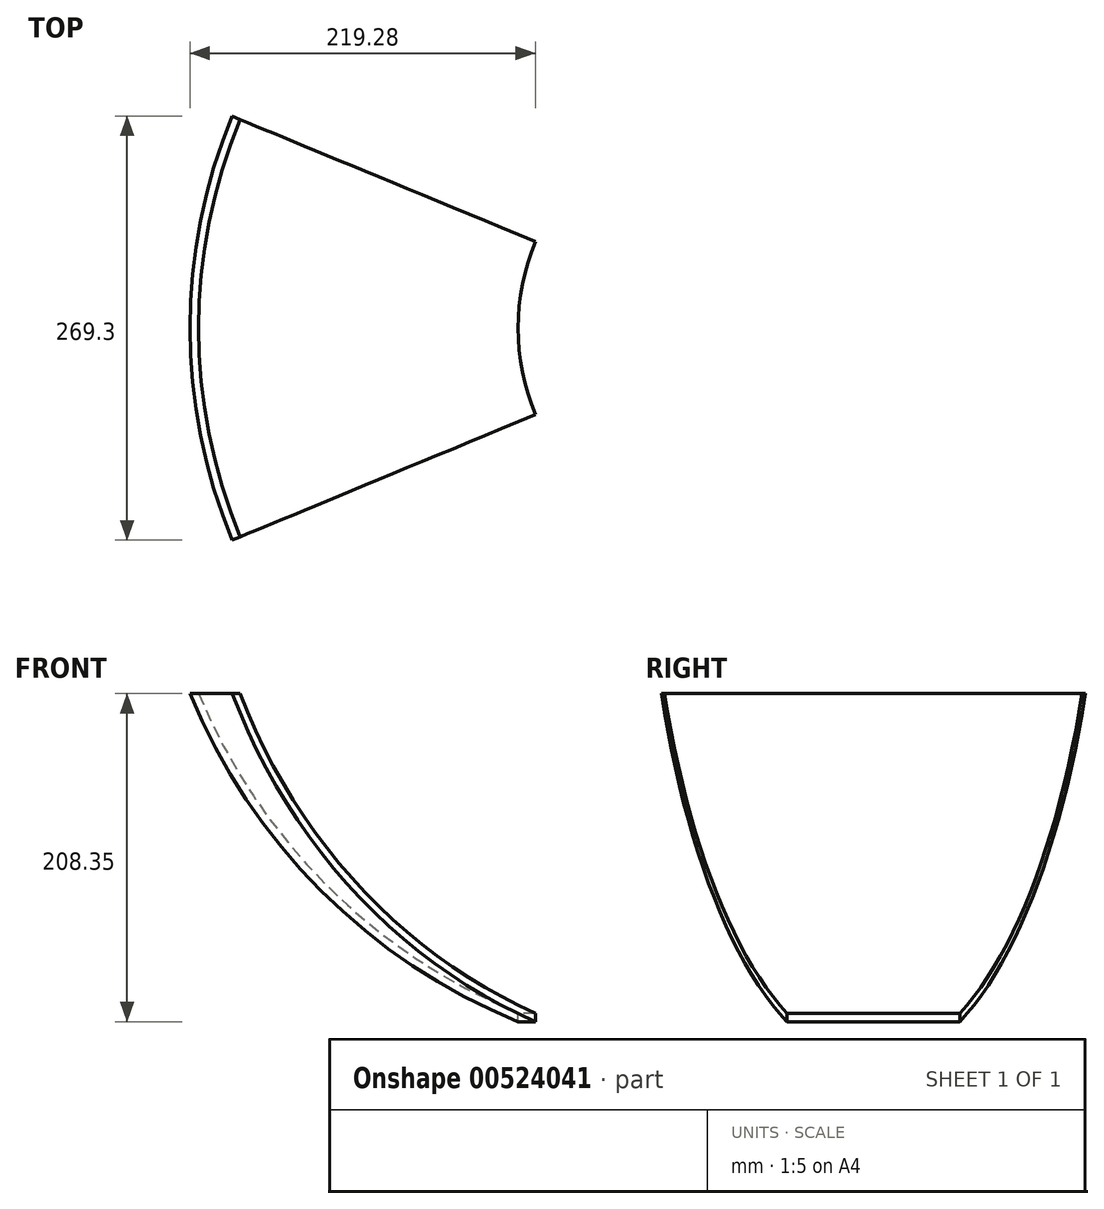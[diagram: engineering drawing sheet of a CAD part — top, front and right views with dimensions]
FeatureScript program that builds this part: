
annotation { "Feature Type Name" : "Feature", "Feature Type Description" : "" }
export const myFeature = defineFeature(function(context is Context, id is Id, definition is map)
    precondition{}
    {
        {
            var Q0;
            Q0=qCreatedBy(makeId("Front.planeOp"),FACE);
            var sketch = newSketch(context, id + "F0", { "sketchPlane" : qUnion([Q0])});
            skArc(sketch, "E0", {"start": v(-375, 0) * mm, "mid": v(-265.17, -265.17) * mm, "end": v(0, -375) * mm});
            skLineSegment(sketch, "E1", {"start": v(0, 0) * mm, "end": v(-375, 0) * mm});
            skLineSegment(sketch, "E2.1.0", {"start": v(0, 0) * mm, "end": v(-351.07, -145.42) * mm});
            skLineSegment(sketch, "E2.2.0", {"start": v(0, 0) * mm, "end": v(-268.7, -268.7) * mm});
            skLineSegment(sketch, "E2.3.0", {"start": v(0, 0) * mm, "end": v(-145.42, -351.07) * mm});
            skLineSegment(sketch, "E2.4.0", {"start": v(0, 0) * mm, "end": v(0, -375) * mm});
            skArc(sketch, "E3.0", {"start": v(-380, 0) * mm, "mid": v(-268.7, -268.7) * mm, "end": v(0, -380) * mm});
            skPoint(sketch, "E4.orphan", {"position": v(-346.45, -143.5) * mm});
            skPoint(sketch, "E5.orphan", {"position": v(-265.17, -265.17) * mm});
            skPoint(sketch, "E6.orphan", {"position": v(-143.5, -346.45) * mm});
            skLineSegment(sketch, "E7", {"start": v(-346.45, -143.5) * mm, "end": v(-351.86, -143.5) * mm});
            skLineSegment(sketch, "E8", {"start": v(-143.5, -346.45) * mm, "end": v(-143.5, -351.86) * mm});
            skSolve(sketch);
        }
        {
            var Q0;
            {var subQ3=sQuery(id+"F0.wireOp",EDGE,"E7");Q0=makeQuery(id+"F0.imprint","IMPRINT",FACE,{"disambiguationData":[TD([[makeQuery(id+"F0.imprint","IMPRINT",EDGE,{"derivedFrom":subQ3}),1.0]])]});}
            var Q1;
            {var subQ3=sQuery(id+"F0.wireOp",EDGE,"E2.2.0");var subQ5=sQuery(id+"F0.wireOp",EDGE,"E3.0");var subQ7=makeQuery(id+"F0.imprint","INTERSECT",VERTEX,{"derivedFrom":[subQ3,subQ5]});Q1=makeQuery(id+"F0.imprint","IMPRINT",FACE,{"disambiguationData":[TD([[makeQuery(id+"F0.imprint","IMPRINT",EDGE,{"disambiguationData":[TD([[subQ7,1.0]])],"derivedFrom":subQ3}),-1.0]])]});}
            var Q2;
            {var subQ3=sQuery(id+"F0.wireOp",EDGE,"E2.2.0");var subQ5=sQuery(id+"F0.wireOp",EDGE,"E3.0");var subQ6=makeQuery(id+"F0.imprint","INTERSECT",VERTEX,{"derivedFrom":[subQ3,subQ5]});Q2=makeQuery(id+"F0.imprint","IMPRINT",FACE,{"disambiguationData":[TD([[makeQuery(id+"F0.imprint","IMPRINT",EDGE,{"disambiguationData":[TD([[subQ6,1.0]])],"derivedFrom":subQ3}),1.0]])]});}
            var Q3;
            {var subQ3=sQuery(id+"F0.wireOp",EDGE,"E8");Q3=makeQuery(id+"F0.imprint","IMPRINT",FACE,{"disambiguationData":[TD([[makeQuery(id+"F0.imprint","IMPRINT",EDGE,{"derivedFrom":subQ3}),-1.0]])]});}
            var Q4;
            Q4=sQuery(id+"F0.wireOp",EDGE,"E2.4.0");
            revolve(context, id + "F1", {"entities" : qUnion([Q0, Q1, Q2, Q3]), "axis" : qUnion([Q4]), "revolveType" : RevolveType.ONE_DIRECTION, "angle" : 22.5 * degree});
        }
        {
            var Q0;
            Q0=makeQuery(id+"F1.opRevolve","SWEPT_BODY",BODY,{"disambiguationData":[OSD([sQuery(id+"F0.wireOp",EDGE,"E0"),sQuery(id+"F0.wireOp",EDGE,"E3.0"),sQuery(id+"F0.wireOp",EDGE,"E7"),sQuery(id+"F0.wireOp",EDGE,"E8")])]});
            var Q1;
            {var subQ0=sQuery(id+"F0.wireOp",EDGE,"E1");Q1=makeQuery(id+"F0.imprint","IMPRINT",FACE,{"disambiguationData":[TD([[makeQuery(id+"F0.imprint","IMPRINT",EDGE,{"derivedFrom":subQ0}),1.0]])]});}
            mirror(context, id + "F2", {"operationType" : NewBodyOperationType.ADD, "entities" : qUnion([Q0]), "mirrorPlane" : qUnion([Q1])});
        }
        {
            var Q0;
            Q0=sQuery(id+"F0.wireOp",EDGE,"E2.2.0");
            var Q1;
            Q1=sQuery(id+"F0.wireOp",VERTEX,"E0.center");
            cPlane(context, id + "F3", {"entities" : qUnion([Q0, Q1]), "cplaneType" : CPlaneType.CURVE_POINT, "offset" : 25 * mm, "width" : 150 * mm, "height" : 150 * mm});
        }
    });
